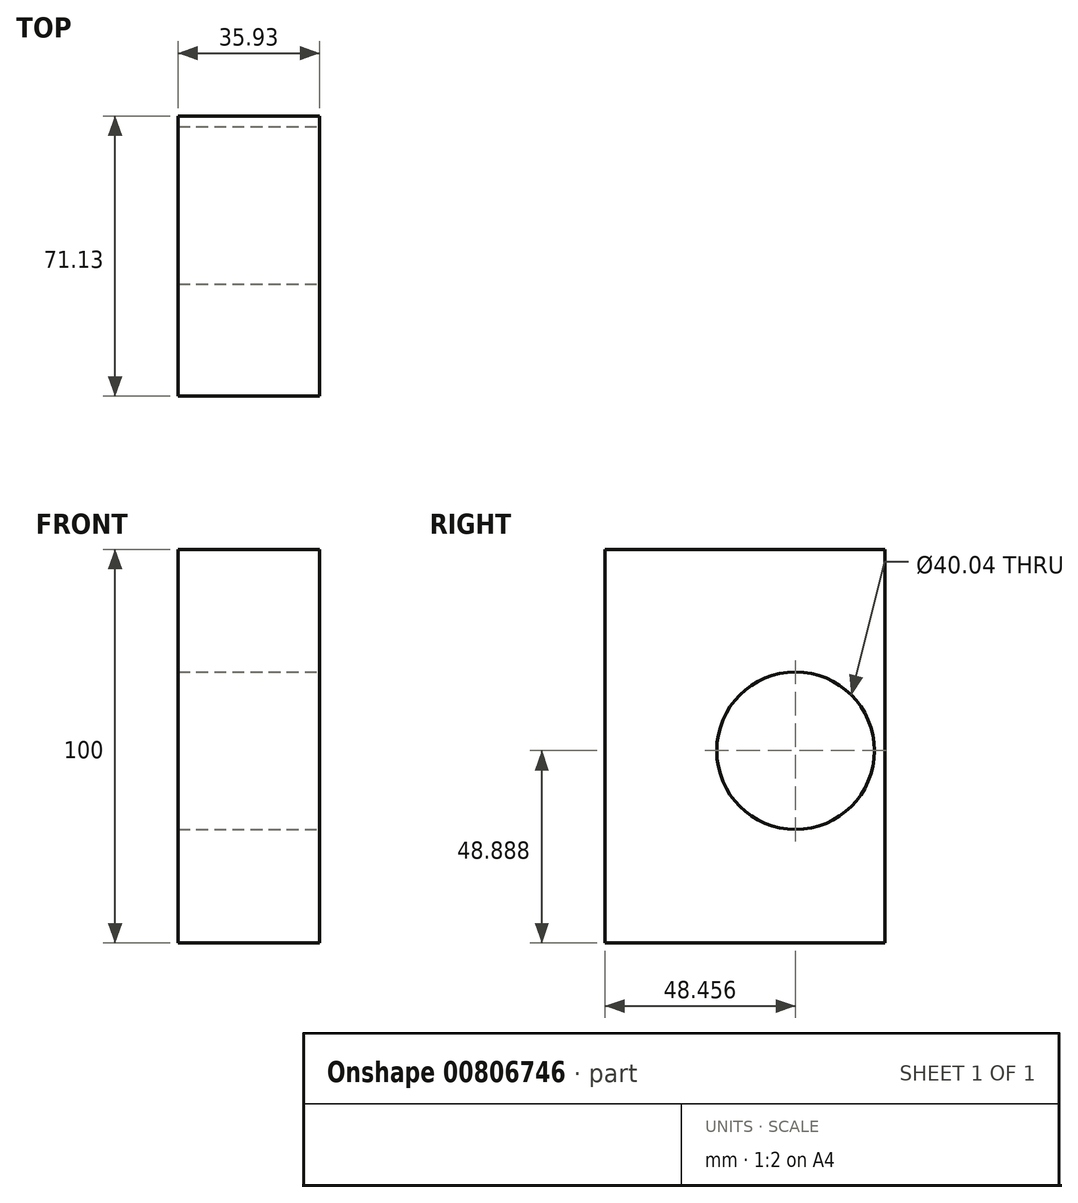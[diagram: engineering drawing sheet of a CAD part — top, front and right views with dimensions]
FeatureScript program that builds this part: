
annotation { "Feature Type Name" : "Feature", "Feature Type Description" : "" }
export const myFeature = defineFeature(function(context is Context, id is Id, definition is map)
    precondition{}
    {
        {
            var Q0;
            Q0=qCreatedBy(makeId("Top.planeOp"),FACE);
            var sketch = newSketch(context, id + "F0", { "sketchPlane" : qUnion([Q0])});
            skLineSegment(sketch, "E0.bottom", {"start": v(-24.4, 34.93) * mm, "end": v(11.52, 34.93) * mm});
            skLineSegment(sketch, "E0.top", {"start": v(-24.4, -36.2) * mm, "end": v(11.52, -36.2) * mm});
            skLineSegment(sketch, "E0.left", {"start": v(-24.4, 34.93) * mm, "end": v(-24.4, -36.2) * mm});
            skLineSegment(sketch, "E0.right", {"start": v(11.52, 34.93) * mm, "end": v(11.52, -36.2) * mm});
            skSolve(sketch);
        }
        {
            var Q0;
            Q0=makeQuery(id+"F0.imprint","IMPRINT",FACE,{"disambiguationData":[TD([[makeQuery(id+"F0.imprint","IMPRINT",EDGE,{"derivedFrom":sQuery(id+"F0.wireOp",EDGE,"E0.bottom")}),-1.0]])]});
            extrude(context, id + "F1", {"entities" : qUnion([Q0]), "depth" : 100 * mm, "offsetDistance" : 25 * mm});
        }
        {
            var Q0;
            Q0=makeQuery(id+"F1.opExtrude","SWEPT_FACE",FACE,{"disambiguationData":[OSD([sQuery(id+"F0.wireOp",EDGE,"E0.top")])]});
            var sketch = newSketch(context, id + "F2", { "sketchPlane" : qUnion([Q0])});
            skLineSegment(sketch, "E1.bottom", {"start": v(-24.4, 67.63) * mm, "end": v(11.52, 67.63) * mm});
            skLineSegment(sketch, "E1.top", {"start": v(-24.4, 28.66) * mm, "end": v(11.52, 28.66) * mm});
            skLineSegment(sketch, "E1.left", {"start": v(-24.4, 67.63) * mm, "end": v(-24.4, 28.66) * mm});
            skLineSegment(sketch, "E1.right", {"start": v(11.52, 67.63) * mm, "end": v(11.52, 28.66) * mm});
            skSolve(sketch);
        }
        {
            var Q0;
            Q0=makeQuery(id+"F1.opExtrude","SWEPT_FACE",FACE,{"disambiguationData":[OSD([sQuery(id+"F0.wireOp",EDGE,"E0.right")])]});
            var sketch = newSketch(context, id + "F3", { "sketchPlane" : qUnion([Q0])});
            skCircle(sketch, "E2", {"center": v(12.26, 48.89) * mm, "radius": 20.02 * mm});
            skSolve(sketch);
        }
        {
            var Q0;
            Q0=makeQuery(id+"F3.imprint","IMPRINT",FACE,{"disambiguationData":[TD([[makeQuery(id+"F3.imprint","IMPRINT",EDGE,{"derivedFrom":sQuery(id+"F3.wireOp",EDGE,"E2")}),1.0]])]});
            extrude(context, id + "F4", {"entities" : qUnion([Q0]), "operationType" : NewBodyOperationType.REMOVE, "oppositeDirection" : true, "depth" : 100 * mm, "offsetDistance" : 25 * mm});
        }
    });
